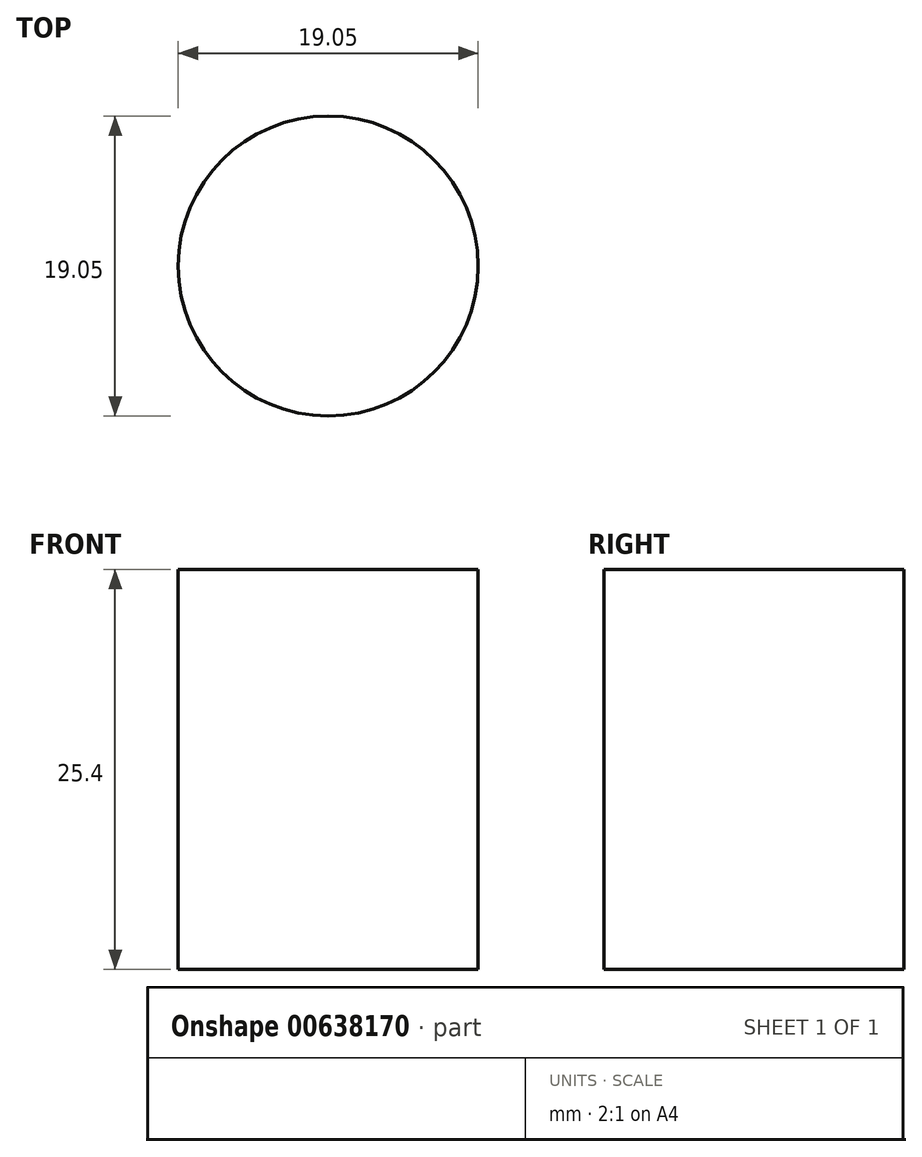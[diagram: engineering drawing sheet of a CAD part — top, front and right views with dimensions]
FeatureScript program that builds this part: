
annotation { "Feature Type Name" : "Feature", "Feature Type Description" : "" }
export const myFeature = defineFeature(function(context is Context, id is Id, definition is map)
    precondition{}
    {
        {
            var Q0;
            Q0=qCreatedBy(makeId("Top.planeOp"),FACE);
            var sketch = newSketch(context, id + "F0", { "sketchPlane" : qUnion([Q0])});
            skCircle(sketch, "E0", {"center": v(-16.01, 9.54) * mm, "radius": 9.53 * mm});
            skSolve(sketch);
        }
        {
            var Q0;
            Q0=makeQuery(id+"F0.imprint","IMPRINT",FACE,{"disambiguationData":[TD([[makeQuery(id+"F0.imprint","IMPRINT",EDGE,{"derivedFrom":sQuery(id+"F0.wireOp",EDGE,"E0")}),1.0]])]});
            extrude(context, id + "F1", {"entities" : qUnion([Q0]), "depth" : 25.4 * mm, "offsetDistance" : 25.4 * mm});
        }
    });
